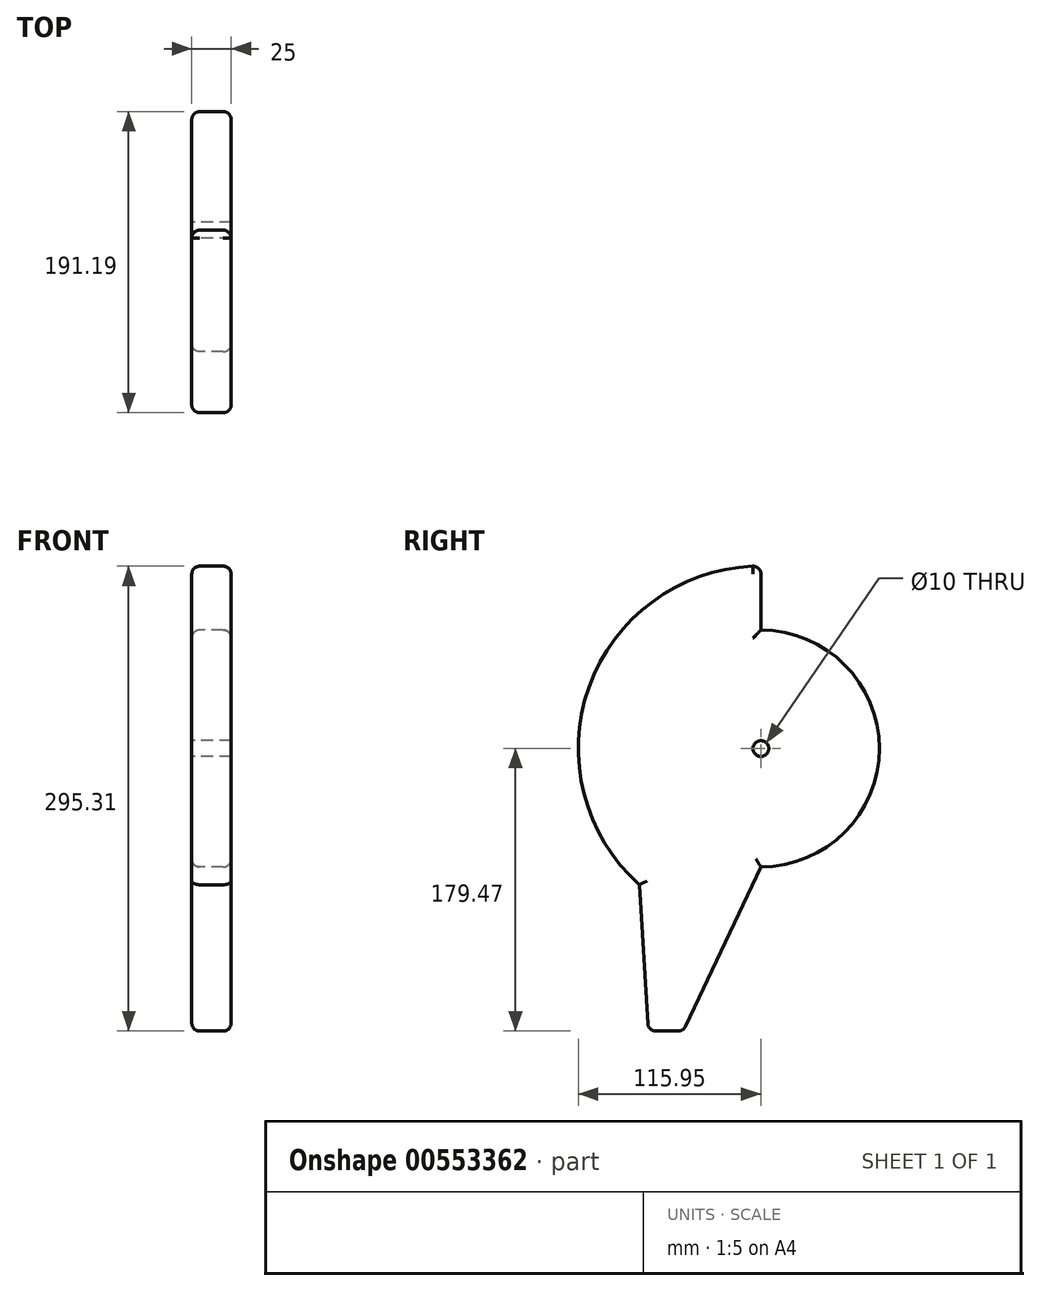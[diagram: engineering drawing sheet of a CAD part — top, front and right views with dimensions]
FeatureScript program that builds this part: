
annotation { "Feature Type Name" : "Feature", "Feature Type Description" : "" }
export const myFeature = defineFeature(function(context is Context, id is Id, definition is map)
    precondition{}
    {
        {
            var Q0;
            Q0=qCreatedBy(makeId("Right.planeOp"),FACE);
            var sketch = newSketch(context, id + "F0", { "sketchPlane" : qUnion([Q0])});
            skArc(sketch, "E0", {"start": v(0, 75.24) * mm, "mid": v(75.24, 0) * mm, "end": v(0, -75.24) * mm});
            skArc(sketch, "E1", {"start": v(0, 115.95) * mm, "mid": v(-108.34, 41.32) * mm, "end": v(-77.21, -86.5) * mm});
            skLineSegment(sketch, "E2", {"start": v(0, 115.95) * mm, "end": v(0, 75.24) * mm});
            skLineSegment(sketch, "E3", {"start": v(0, -75.24) * mm, "end": v(-49.3, -179.47) * mm});
            skLineSegment(sketch, "E4", {"start": v(-49.3, -179.47) * mm, "end": v(-71.5, -179.47) * mm});
            skLineSegment(sketch, "E5", {"start": v(-71.5, -179.47) * mm, "end": v(-77.21, -86.5) * mm});
            skSolve(sketch);
        }
        {
            var Q0;
            Q0 = qSketchRegion(id + "F0", true);
            var Q1;
            Q1=makeQuery(id+"F0.imprint","IMPRINT",FACE,{"disambiguationData":[TD([[makeQuery(id+"F0.imprint","IMPRINT",EDGE,{"derivedFrom":sQuery(id+"F0.wireOp",EDGE,"E0")}),-1.0]])]});
            extrude(context, id + "F1", {"entities" : qUnion([Q0, Q1]), "depth" : 25 * mm, "offsetDistance" : 25 * mm});
        }
        {
            var Q0;
            Q0=makeQuery(id+"F1.opExtrude","CAP_EDGE",EDGE,{"disambiguationData":[OSD([sQuery(id+"F0.wireOp",EDGE,"E2")])],"isStart":false});
            var Q1;
            Q1=makeQuery(id+"F1.opExtrude","CAP_EDGE",EDGE,{"disambiguationData":[OSD([sQuery(id+"F0.wireOp",EDGE,"E2")])],"isStart":true});
            var Q2;
            Q2=makeQuery(id+"F1.opExtrude","SWEPT_EDGE",EDGE,{"disambiguationData":[OSD([sQuery(id+"F0.wireOp",EDGE,"E1"),sQuery(id+"F0.wireOp",EDGE,"E2")])]});
            var Q3;
            Q3=makeQuery(id+"F1.opExtrude","CAP_EDGE",EDGE,{"disambiguationData":[OSD([sQuery(id+"F0.wireOp",EDGE,"E5")])],"isStart":true});
            var Q4;
            Q4=makeQuery(id+"F1.opExtrude","CAP_EDGE",EDGE,{"disambiguationData":[OSD([sQuery(id+"F0.wireOp",EDGE,"E5")])],"isStart":false});
            var Q5;
            Q5=makeQuery(id+"F1.opExtrude","CAP_EDGE",EDGE,{"disambiguationData":[OSD([sQuery(id+"F0.wireOp",EDGE,"E4")])],"isStart":true});
            var Q6;
            Q6=makeQuery(id+"F1.opExtrude","SWEPT_EDGE",EDGE,{"disambiguationData":[OSD([sQuery(id+"F0.wireOp",EDGE,"E4"),sQuery(id+"F0.wireOp",EDGE,"E5")])]});
            var Q7;
            Q7=makeQuery(id+"F1.opExtrude","CAP_EDGE",EDGE,{"disambiguationData":[OSD([sQuery(id+"F0.wireOp",EDGE,"E4")])],"isStart":false});
            var Q8;
            Q8=makeQuery(id+"F1.opExtrude","CAP_EDGE",EDGE,{"disambiguationData":[OSD([sQuery(id+"F0.wireOp",EDGE,"E3")])],"isStart":false});
            var Q9;
            Q9=makeQuery(id+"F1.opExtrude","CAP_EDGE",EDGE,{"disambiguationData":[OSD([sQuery(id+"F0.wireOp",EDGE,"E3")])],"isStart":true});
            var Q10;
            Q10=makeQuery(id+"F1.opExtrude","SWEPT_EDGE",EDGE,{"disambiguationData":[OSD([sQuery(id+"F0.wireOp",EDGE,"E3"),sQuery(id+"F0.wireOp",EDGE,"E4")])]});
            fillet(context, id + "F2", {"entities" : qUnion([Q0, Q1, Q2, Q3, Q4, Q5, Q6, Q7, Q8, Q9, Q10]), "radius" : 5 * mm, "tangentPropagation" : true, "allowEdgeOverflow" : false});
        }
        {
            var Q0;
            Q0=makeQuery(id+"F1.opExtrude","CAP_EDGE",EDGE,{"disambiguationData":[OSD([sQuery(id+"F0.wireOp",EDGE,"E0")])],"isStart":false});
            var Q1;
            Q1=makeQuery(id+"F1.opExtrude","CAP_EDGE",EDGE,{"disambiguationData":[OSD([sQuery(id+"F0.wireOp",EDGE,"E1")])],"isStart":false});
            var Q2;
            Q2=makeQuery(id+"F1.opExtrude","CAP_EDGE",EDGE,{"disambiguationData":[OSD([sQuery(id+"F0.wireOp",EDGE,"E1")])],"isStart":true});
            var Q3;
            Q3=makeQuery(id+"F1.opExtrude","CAP_EDGE",EDGE,{"disambiguationData":[OSD([sQuery(id+"F0.wireOp",EDGE,"E0")])],"isStart":true});
            fillet(context, id + "F3", {"entities" : qUnion([Q0, Q1, Q2, Q3]), "radius" : 5 * mm, "tangentPropagation" : true, "allowEdgeOverflow" : false});
        }
        {
            var Q0;
            Q0=makeQuery(id+"F1.opExtrude","CAP_FACE",FACE,{"disambiguationData":[OSD([sQuery(id+"F0.wireOp",EDGE,"E0"),sQuery(id+"F0.wireOp",EDGE,"E1"),sQuery(id+"F0.wireOp",EDGE,"E2"),sQuery(id+"F0.wireOp",EDGE,"E3"),sQuery(id+"F0.wireOp",EDGE,"E4"),sQuery(id+"F0.wireOp",EDGE,"E5")])],"isStart":true});
            var sketch = newSketch(context, id + "F4", { "sketchPlane" : qUnion([Q0])});
            skPoint(sketch, "E6", {"position": v(0, 0) * mm});
            skSolve(sketch);
        }
        {
            var Q0;
            Q0=sQuery(id+"F4.wireOp",VERTEX,"E6");
            var Q1;
            Q1=makeQuery(id+"F1.opExtrude","SWEPT_BODY",BODY,{"disambiguationData":[OSD([sQuery(id+"F0.wireOp",EDGE,"E0"),sQuery(id+"F0.wireOp",EDGE,"E1"),sQuery(id+"F0.wireOp",EDGE,"E2"),sQuery(id+"F0.wireOp",EDGE,"E3"),sQuery(id+"F0.wireOp",EDGE,"E4"),sQuery(id+"F0.wireOp",EDGE,"E5")])]});
            hole(context, id + "F5", {"style" : HoleStyle.SIMPLE, "endStyle" : HoleEndStyle.THROUGH, "holeDiameter" : 10 * mm, "isTappedThrough" : true, "tappedDepth" : 12 * mm, "tapClearance" : 3, "locations" : qUnion([Q0]), "scope" : qUnion([Q1])});
        }
    });
